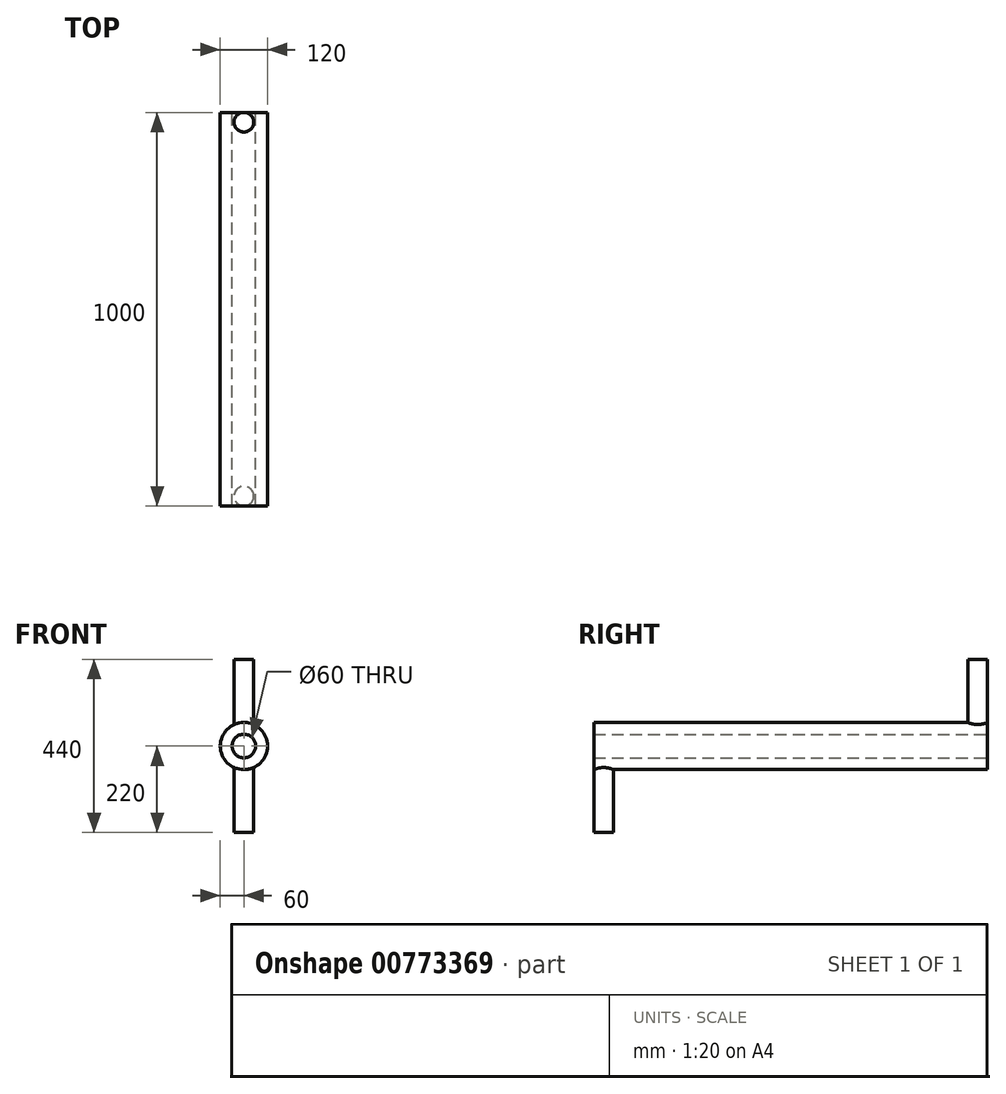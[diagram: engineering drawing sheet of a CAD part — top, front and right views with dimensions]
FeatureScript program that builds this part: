
annotation { "Feature Type Name" : "Feature", "Feature Type Description" : "" }
export const myFeature = defineFeature(function(context is Context, id is Id, definition is map)
    precondition{}
    {
        {
            var Q0;
            Q0=qCreatedBy(makeId("Front.planeOp"),FACE);
            var sketch = newSketch(context, id + "F0", { "sketchPlane" : qUnion([Q0])});
            skCircle(sketch, "E0", {"center": v(0, 0) * mm, "radius": 60 * mm});
            skSolve(sketch);
        }
        {
            var Q0;
            Q0=makeQuery(id+"F0.imprint","IMPRINT",FACE,{"disambiguationData":[TD([[makeQuery(id+"F0.imprint","IMPRINT",EDGE,{"derivedFrom":sQuery(id+"F0.wireOp",EDGE,"E0")}),1.0]])]});
            extrude(context, id + "F1", {"entities" : qUnion([Q0]), "depth" : 1000 * mm, "offsetDistance" : 25 * mm});
        }
        {
            var Q0;
            Q0=qCreatedBy(makeId("Front.planeOp"),FACE);
            var sketch = newSketch(context, id + "F2", { "sketchPlane" : qUnion([Q0])});
            skCircle(sketch, "E1", {"center": v(0, 0) * mm, "radius": 30 * mm});
            skSolve(sketch);
        }
        {
            var Q0;
            Q0 = qSketchRegion(id + "F2", true);
            extrude(context, id + "F3", {"entities" : qUnion([Q0]), "operationType" : NewBodyOperationType.REMOVE, "oppositeDirection" : true, "depth" : -1000 * mm, "offsetDistance" : 25 * mm});
        }
        {
            var Q0;
            Q0=qCreatedBy(makeId("Front.planeOp"),FACE);
            var sketch = newSketch(context, id + "F4", { "sketchPlane" : qUnion([Q0])});
            skLineSegment(sketch, "E2", {"start": v(0, 0) * mm, "end": v(0, 60) * mm});
            skSolve(sketch);
        }
        {
            var Q0;
            Q0=qCreatedBy(makeId("Top.planeOp"),FACE);
            var sketch = newSketch(context, id + "F5", { "sketchPlane" : qUnion([Q0])});
            skCircle(sketch, "E3", {"center": v(0, -25) * mm, "radius": 25 * mm});
            skSolve(sketch);
        }
        {
            var Q0;
            Q0 = qSketchRegion(id + "F5", true);
            extrude(context, id + "F6", {"entities" : qUnion([Q0]), "operationType" : NewBodyOperationType.ADD, "depth" : 220 * mm, "offsetDistance" : 25 * mm});
        }
        {
            var Q0;
            Q0=sQuery(id+"F4.wireOp",VERTEX,"E2.start");
            var Q1;
            Q1=makeQuery(id+"F6.opExtrude","SWEPT_BODY",BODY,{"disambiguationData":[OSD([sQuery(id+"F5.wireOp",EDGE,"E3")])]});
            var Q2;
            Q2=makeQuery(id+"F1.opExtrude","SWEPT_BODY",BODY,{"disambiguationData":[OSD([sQuery(id+"F0.wireOp",EDGE,"E0")])]});
            hole(context, id + "F7", {"style" : HoleStyle.SIMPLE, "endStyle" : HoleEndStyle.THROUGH, "oppositeDirection" : true, "holeDiameter" : 60 * mm, "majorDiameter" : 5 * mm, "isTappedThrough" : true, "tappedDepth" : 12 * mm, "tapClearance" : 3, "locations" : qUnion([Q0]), "scope" : qUnion([Q1, Q2])});
        }
        {
            var Q0;
            Q0=qCreatedBy(makeId("Top.planeOp"),FACE);
            var sketch = newSketch(context, id + "F8", { "sketchPlane" : qUnion([Q0])});
            skLineSegment(sketch, "E4", {"start": v(0, 0) * mm, "end": v(0, -950) * mm});
            skPoint(sketch, "E5", {"position": v(0, -1000) * mm});
            skPoint(sketch, "E6", {"position": v(0, -975) * mm});
            skCircle(sketch, "E7", {"center": v(0, -975) * mm, "radius": 25 * mm});
            skSolve(sketch);
        }
        {
            var Q0;
            Q0 = qSketchRegion(id + "F8", true);
            extrude(context, id + "F9", {"entities" : qUnion([Q0]), "operationType" : NewBodyOperationType.ADD, "oppositeDirection" : true, "depth" : 220 * mm, "offsetDistance" : 25 * mm});
        }
        {
            var Q0;
            Q0=qCreatedBy(makeId("Front.planeOp"),FACE);
            var sketch = newSketch(context, id + "F10", { "sketchPlane" : qUnion([Q0])});
            skPoint(sketch, "E8", {"position": v(0, 0) * mm});
            skCircle(sketch, "E9", {"center": v(0, 0) * mm, "radius": 30 * mm});
            skSolve(sketch);
        }
        {
            var Q0;
            Q0 = qSketchRegion(id + "F10", true);
            extrude(context, id + "F11", {"entities" : qUnion([Q0]), "operationType" : NewBodyOperationType.REMOVE, "depth" : 1000 * mm, "offsetDistance" : 25 * mm});
        }
    });
